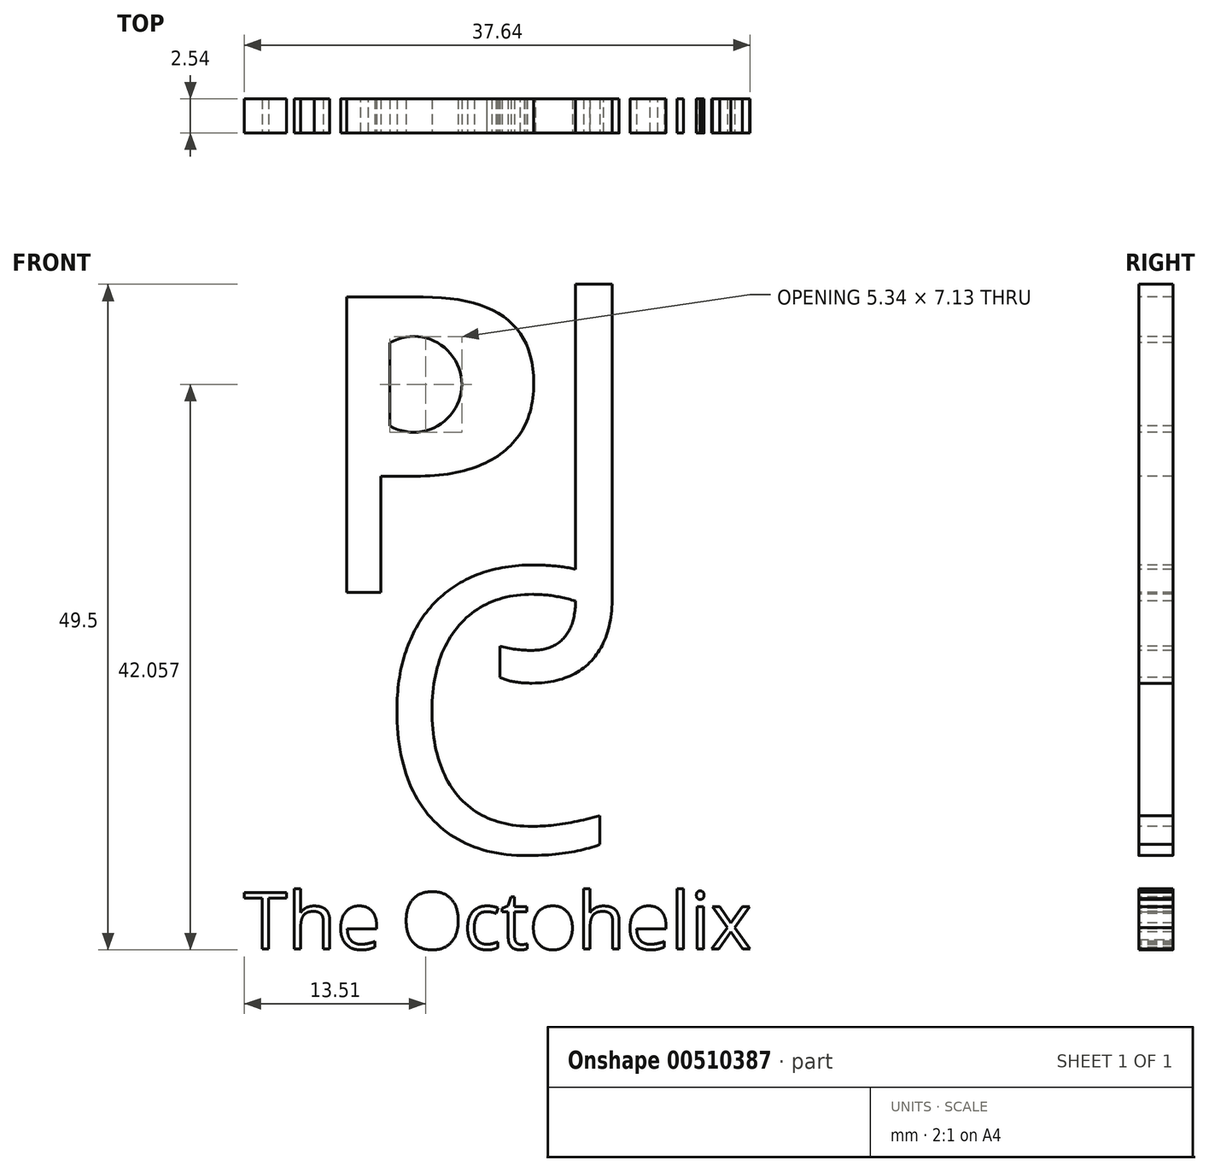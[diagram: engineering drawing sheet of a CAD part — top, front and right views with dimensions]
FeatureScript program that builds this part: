
annotation { "Feature Type Name" : "Feature", "Feature Type Description" : "" }
export const myFeature = defineFeature(function(context is Context, id is Id, definition is map)
    precondition{}
    {
        {
            var Q0;
            Q0=qCreatedBy(makeId("Front.planeOp"),FACE);
            var sketch = newSketch(context, id + "F0", { "sketchPlane" : qUnion([Q0])});
            skLineSegment(sketch, "E0.bottom", {"start": v(-40.48, 30.36) * mm, "end": v(40.67, 30.36) * mm});
            skLineSegment(sketch, "E0.top", {"start": v(-40.48, -27.88) * mm, "end": v(40.67, -27.88) * mm});
            skLineSegment(sketch, "E0.left", {"start": v(-40.48, 30.36) * mm, "end": v(-40.48, -27.88) * mm});
            skLineSegment(sketch, "E0.right", {"start": v(40.67, 30.36) * mm, "end": v(40.67, -27.88) * mm});
            skSolve(sketch);
        }
        {
            var Q0;
            Q0=makeQuery(id+"F0.imprint","IMPRINT",FACE,{"disambiguationData":[TD([[makeQuery(id+"F0.imprint","IMPRINT",EDGE,{"derivedFrom":sQuery(id+"F0.wireOp",EDGE,"E0.bottom")}),-1.0]])]});
            extrude(context, id + "F1", {"entities" : qUnion([Q0]), "depth" : 2.54 * mm});
        }
        {
            var Q0;
            Q0=makeQuery(id+"F1.opExtrude","CAP_FACE",FACE,{"disambiguationData":[OSD([sQuery(id+"F0.wireOp",EDGE,"E0.bottom"),sQuery(id+"F0.wireOp",EDGE,"E0.top"),sQuery(id+"F0.wireOp",EDGE,"E0.left"),sQuery(id+"F0.wireOp",EDGE,"E0.right")])],"isStart":false});
            var sketch = newSketch(context, id + "F2", { "sketchPlane" : qUnion([Q0])});
            skText(sketch, "E1", { "text": "P", "fontName": "OpenSans-Regular.ttf"});
            skText(sketch, "E2", { "text": "J", "fontName": "OpenSans-Regular.ttf"});
            skText(sketch, "E3", { "text": "C", "fontName": "OpenSans-Regular.ttf"});
            skText(sketch, "E4", { "text": "The Octohelix", "fontName": "OpenSans-Regular.ttf"});
            const initialGuessF2  = {"E1": [-0.01547, 0.00057, 1, 0, 0.02215], "E2": [0.00153, 0, 1, 0, 0.02368], "E3": [-0.0105, -0.01871, 1, 0, 0.0212], "E4": [-0.02011, -0.02596, 1, 0, 0.00425]};
            skSetInitialGuess(sketch, initialGuessF2);
            skSolve(sketch);
        }
        {
            var Q0;
            Q0=makeQuery(id+"F2.imprint","IMPRINT",FACE,{"disambiguationData":[TD([[makeQuery(id+"F2.imprint","IMPRINT",EDGE,{"derivedFrom":sQuery(id+"F2.wireOp",EDGE,"E1.sketch_text.stroke-0")}),1.0]])]});
            extrude(context, id + "F3", {"entities" : qUnion([Q0]), "operationType" : NewBodyOperationType.REMOVE, "oppositeDirection" : true, "depth" : 25.4 * mm});
        }
        {
            var Q0;
            Q0=makeQuery(id+"F3.boolean.opBoolean","SPLIT",FACE,{"disambiguationData":[TD([makeQuery(id+"F3.opExtrude","SWEPT_FACE",FACE,{"disambiguationData":[OSD([sQuery(id+"F2.wireOp",EDGE,"E1.sketch_text.stroke-0")])]})])],"derivedFrom":makeQuery(id+"F1.opExtrude","CAP_FACE",FACE,{"disambiguationData":[OSD([sQuery(id+"F0.wireOp",EDGE,"E0.bottom"),sQuery(id+"F0.wireOp",EDGE,"E0.top"),sQuery(id+"F0.wireOp",EDGE,"E0.left"),sQuery(id+"F0.wireOp",EDGE,"E0.right")])],"isStart":false})});
            var sketch = newSketch(context, id + "F4", { "sketchPlane" : qUnion([Q0])});
            skLineSegment(sketch, "E5", {"start": v(-9.22, 12.95) * mm, "end": v(-9.22, 19.13) * mm});
            skArc(sketch, "E6", {"start": v(-9.22, 12.95) * mm, "mid": v(-3.88, 16.04) * mm, "end": v(-9.22, 19.13) * mm});
            skSolve(sketch);
        }
        {
            var Q0;
            Q0=makeQuery(id+"F4.imprint","IMPRINT",FACE,{"disambiguationData":[TD([[makeQuery(id+"F4.imprint","IMPRINT",EDGE,{"derivedFrom":sQuery(id+"F4.wireOp",EDGE,"E5")}),-1.0]])]});
            extrude(context, id + "F5", {"entities" : qUnion([Q0]), "operationType" : NewBodyOperationType.REMOVE, "oppositeDirection" : true, "depth" : 25.4 * mm});
        }
    });
